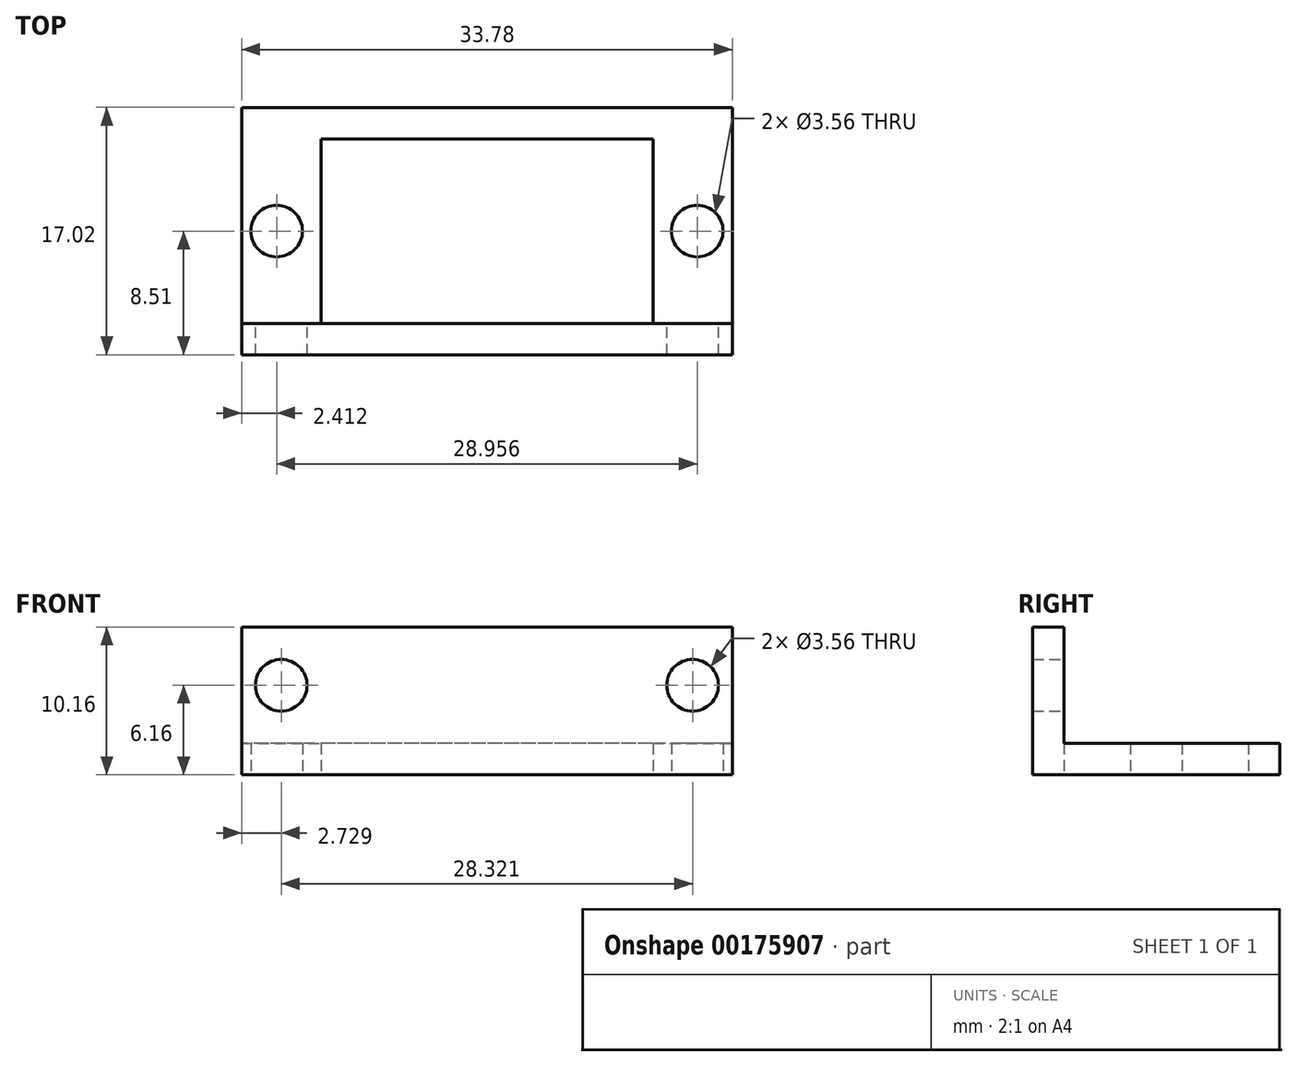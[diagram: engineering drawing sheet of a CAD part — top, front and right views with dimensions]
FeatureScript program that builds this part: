
annotation { "Feature Type Name" : "Feature", "Feature Type Description" : "" }
export const myFeature = defineFeature(function(context is Context, id is Id, definition is map)
    precondition{}
    {
        {
            var Q0;
            Q0=qCreatedBy(makeId("Top.planeOp"),FACE);
            var sketch = newSketch(context, id + "F0", { "sketchPlane" : qUnion([Q0])});
            skLineSegment(sketch, "E0.bottom", {"start": v(11.43, 6.35) * mm, "end": v(-11.43, 6.35) * mm});
            skLineSegment(sketch, "E0.top", {"start": v(11.43, -6.35) * mm, "end": v(-11.43, -6.35) * mm});
            skLineSegment(sketch, "E0.left", {"start": v(11.43, 6.35) * mm, "end": v(11.43, -6.35) * mm});
            skLineSegment(sketch, "E0.right", {"start": v(-11.43, 6.35) * mm, "end": v(-11.43, -6.35) * mm});
            skPoint(sketch, "E0.middle", {"position": v(0, 0) * mm});
            skLineSegment(sketch, "E1.bottom", {"start": v(16.9, 8.5) * mm, "end": v(-16.9, 8.5) * mm});
            skLineSegment(sketch, "E1.top", {"start": v(16.9, -8.5) * mm, "end": v(-16.9, -8.5) * mm});
            skLineSegment(sketch, "E1.left", {"start": v(16.9, 8.5) * mm, "end": v(16.9, -8.5) * mm});
            skLineSegment(sketch, "E1.right", {"start": v(-16.9, 8.5) * mm, "end": v(-16.9, -8.5) * mm});
            skCircle(sketch, "E2", {"center": v(14.48, 0) * mm, "radius": 1.78 * mm});
            skPoint(sketch, "E2.centerSnap0", {"position": v(11.43, 0) * mm});
            skCircle(sketch, "E3", {"center": v(-14.48, 0) * mm, "radius": 1.78 * mm});
            skSolve(sketch);
        }
        {
            var Q0;
            Q0 = qSketchRegion(id + "F0", true);
            extrude(context, id + "F1", {"entities" : qUnion([Q0]), "depth" : 2.16 * mm});
        }
        {
            var Q0;
            Q0=makeQuery(id+"F1.opExtrude","CAP_FACE",FACE,{"disambiguationData":[OSD([sQuery(id+"F0.wireOp",EDGE,"E0.bottom"),sQuery(id+"F0.wireOp",EDGE,"E0.top"),sQuery(id+"F0.wireOp",EDGE,"E0.left"),sQuery(id+"F0.wireOp",EDGE,"E0.right"),sQuery(id+"F0.wireOp",EDGE,"E1.bottom"),sQuery(id+"F0.wireOp",EDGE,"E1.top"),sQuery(id+"F0.wireOp",EDGE,"E1.left"),sQuery(id+"F0.wireOp",EDGE,"E1.right"),sQuery(id+"F0.wireOp",EDGE,"E2"),sQuery(id+"F0.wireOp",EDGE,"E3")])],"isStart":false});
            var sketch = newSketch(context, id + "F2", { "sketchPlane" : qUnion([Q0])});
            skLineSegment(sketch, "E4.bottom", {"start": v(-16.9, -8.5) * mm, "end": v(16.9, -8.5) * mm});
            skLineSegment(sketch, "E4.top", {"start": v(-16.9, -6.35) * mm, "end": v(16.9, -6.35) * mm});
            skLineSegment(sketch, "E4.left", {"start": v(-16.9, -8.5) * mm, "end": v(-16.9, -6.35) * mm});
            skLineSegment(sketch, "E4.right", {"start": v(16.9, -8.5) * mm, "end": v(16.9, -6.35) * mm});
            skSolve(sketch);
        }
        {
            var Q0;
            Q0 = qSketchRegion(id + "F2", true);
            extrude(context, id + "F3", {"entities" : qUnion([Q0]), "operationType" : NewBodyOperationType.ADD, "depth" : 8 * mm});
        }
        {
            var Q0;
            Q0=makeQuery(id+"F3.boolean.opBoolean","MERGE",FACE,{"derivedFrom":[makeQuery(id+"F1.opExtrude","SWEPT_FACE",FACE,{"disambiguationData":[OSD([sQuery(id+"F0.wireOp",EDGE,"E0.top")])]}),makeQuery(id+"F3.opExtrude","SWEPT_FACE",FACE,{"disambiguationData":[OSD([sQuery(id+"F2.wireOp",EDGE,"E4.top")])]})]});
            var sketch = newSketch(context, id + "F4", { "sketchPlane" : qUnion([Q0])});
            skCircle(sketch, "E5", {"center": v(14.16, 6.16) * mm, "radius": 1.78 * mm});
            skPoint(sketch, "E5.centerSnap0", {"position": v(14.16, 2.16) * mm});
            skCircle(sketch, "E6", {"center": v(-14.16, 6.16) * mm, "radius": 1.78 * mm});
            skPoint(sketch, "E6.centerSnap0", {"position": v(-14.16, 2.16) * mm});
            skSolve(sketch);
        }
        {
            var Q0;
            Q0 = qSketchRegion(id + "F4", true);
            extrude(context, id + "F5", {"entities" : qUnion([Q0]), "operationType" : NewBodyOperationType.REMOVE, "endBound" : BoundingType.THROUGH_ALL, "oppositeDirection" : true, "depth" : 25.4 * mm});
        }
    });
